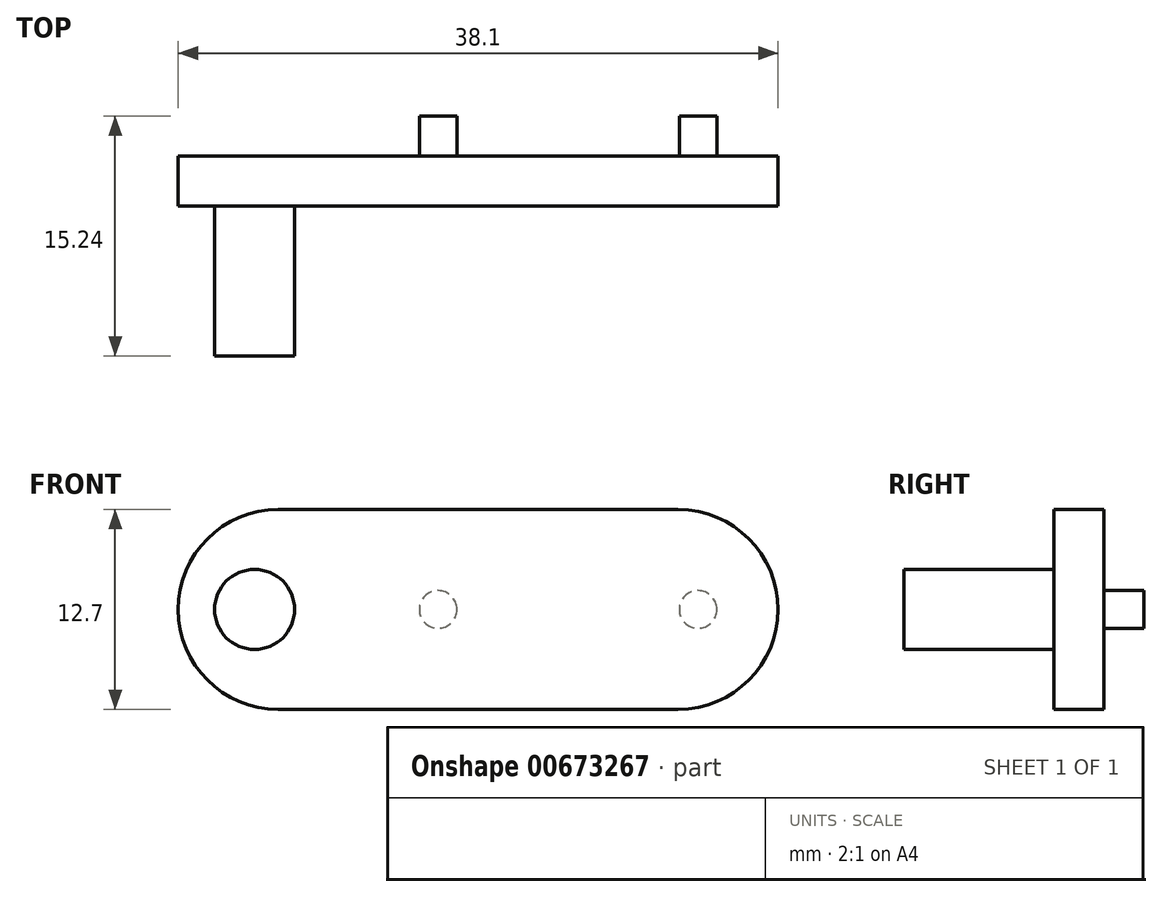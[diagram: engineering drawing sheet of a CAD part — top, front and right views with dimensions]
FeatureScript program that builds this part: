
annotation { "Feature Type Name" : "Feature", "Feature Type Description" : "" }
export const myFeature = defineFeature(function(context is Context, id is Id, definition is map)
    precondition{}
    {
        {
            var Q0;
            Q0=qCreatedBy(makeId("Front.planeOp"),FACE);
            var sketch = newSketch(context, id + "F0", { "sketchPlane" : qUnion([Q0])});
            skArc(sketch, "E0", {"start": v(0, 6.35) * mm, "mid": v(-6.35, 0) * mm, "end": v(0, -6.35) * mm});
            skArc(sketch, "E1", {"start": v(25.4, -6.35) * mm, "mid": v(31.75, 0) * mm, "end": v(25.4, 6.35) * mm});
            skLineSegment(sketch, "E2", {"start": v(0, 6.35) * mm, "end": v(25.4, 6.35) * mm});
            skLineSegment(sketch, "E3", {"start": v(0, -6.35) * mm, "end": v(25.4, -6.35) * mm});
            skSolve(sketch);
        }
        {
            var Q0;
            Q0=qSketchRegion(id+"F0",true);
            extrude(context, id + "F1", {"entities" : qUnion([Q0]), "depth" : 3.17 * mm});
        }
        {
            var Q0;
            Q0=qCreatedBy(makeId("Front.planeOp"),FACE);
            var sketch = newSketch(context, id + "F2", { "sketchPlane" : qUnion([Q0])});
            skCircle(sketch, "E4", {"center": v(10.16, 0) * mm, "radius": 1.2 * mm});
            skCircle(sketch, "E5", {"center": v(26.67, 0) * mm, "radius": 1.2 * mm});
            skSolve(sketch);
        }
        {
            var Q0;
            Q0=qSketchRegion(id+"F2",true);
            extrude(context, id + "F3", {"entities" : qUnion([Q0]), "operationType" : NewBodyOperationType.ADD, "oppositeDirection" : true, "depth" : 2.54 * mm});
        }
        {
            var Q0;
            Q0=qCreatedBy(makeId("Front.planeOp"),FACE);
            var sketch = newSketch(context, id + "F4", { "sketchPlane" : qUnion([Q0])});
            skCircle(sketch, "E6", {"center": v(-1.5, 0) * mm, "radius": 2.54 * mm});
            skSolve(sketch);
        }
        {
            var Q0;
            Q0=qSketchRegion(id+"F4",true);
            extrude(context, id + "F5", {"entities" : qUnion([Q0]), "operationType" : NewBodyOperationType.ADD, "depth" : 12.7 * mm});
        }
    });
